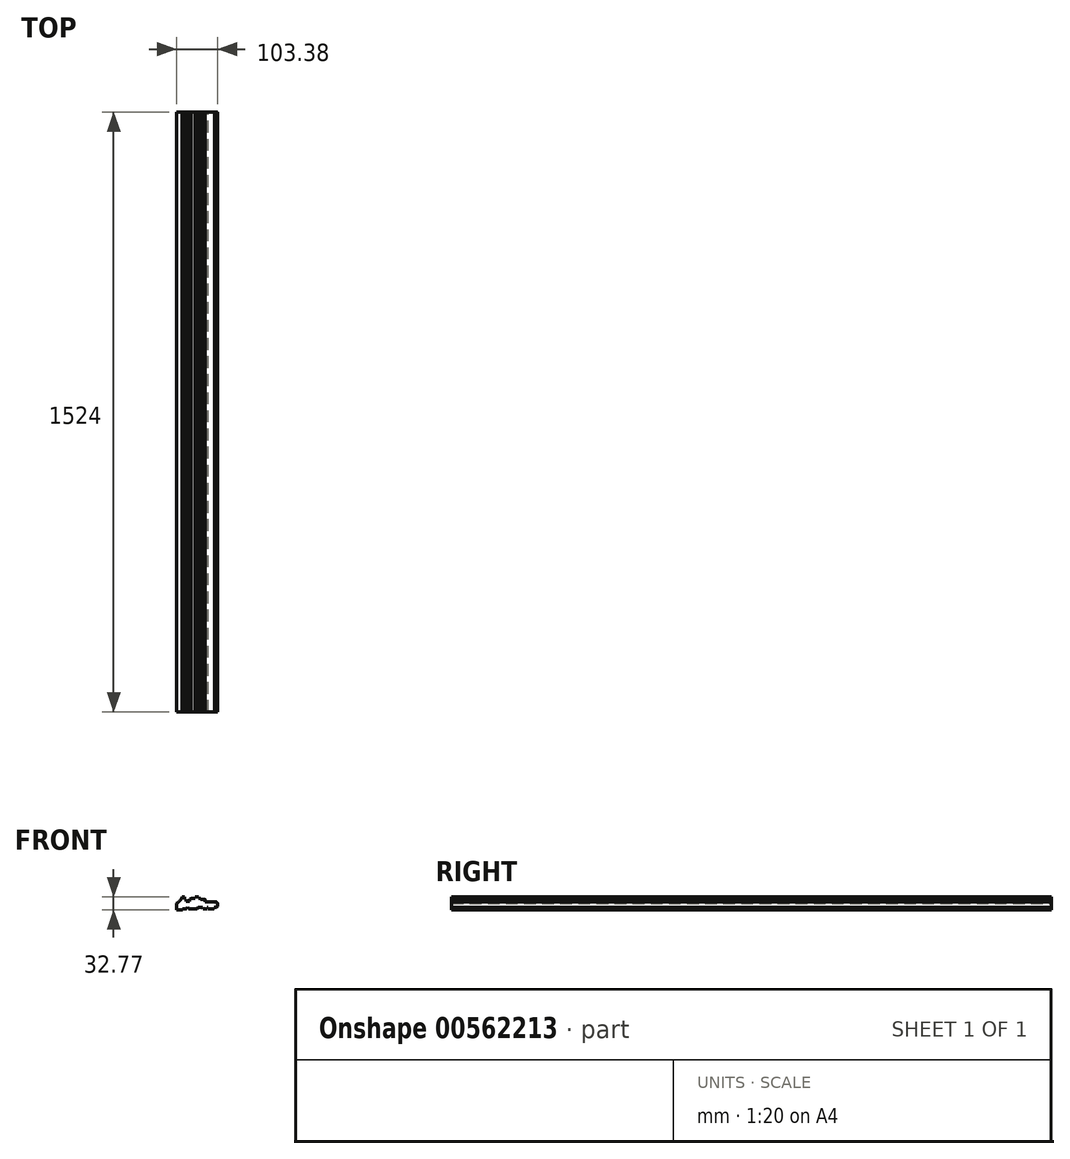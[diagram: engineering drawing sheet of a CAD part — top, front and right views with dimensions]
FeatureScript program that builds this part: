
annotation { "Feature Type Name" : "Feature", "Feature Type Description" : "" }
export const myFeature = defineFeature(function(context is Context, id is Id, definition is map)
    precondition{}
    {
        {
            var Q0;
            Q0=qCreatedBy(makeId("Front.planeOp"),FACE);
            var sketch = newSketch(context, id + "F0", { "sketchPlane" : qUnion([Q0])});
            skLineSegment(sketch, "E0", {"start": v(-88.77, 0) * mm, "end": v(-103.38, 0) * mm});
            skLineSegment(sketch, "E1", {"start": v(-103.38, 0) * mm, "end": v(-103.38, 16.8) * mm});
            skLineSegment(sketch, "E2", {"start": v(-88.77, 0) * mm, "end": v(-88.77, 2.08) * mm});
            skLineSegment(sketch, "E3", {"start": v(-88.77, 2.08) * mm, "end": v(-78.61, 2.08) * mm});
            skArc(sketch, "E4", {"start": v(-103.38, 16.8) * mm, "mid": v(-95.24, 23.3) * mm, "end": v(-90, 32.28) * mm});
            skLineSegment(sketch, "E5", {"start": v(-103.38, 16.8) * mm, "end": v(-90, 32.28) * mm, "construction": true});
            skLineSegment(sketch, "E6", {"start": v(-90, 32.28) * mm, "end": v(-83, 32.28) * mm});
            skLineSegment(sketch, "E7", {"start": v(-83, 32.28) * mm, "end": v(-83, 26.5) * mm});
            skLineSegment(sketch, "E8", {"start": v(-83, 26.5) * mm, "end": v(-80.16, 26.5) * mm});
            skLineSegment(sketch, "E9", {"start": v(-80.16, 26.5) * mm, "end": v(-80.16, 21.59) * mm});
            skLineSegment(sketch, "E10", {"start": v(-80.16, 21.59) * mm, "end": v(-70.38, 21.59) * mm});
            skLineSegment(sketch, "E11", {"start": v(-70.38, 21.59) * mm, "end": v(-70.38, 27.23) * mm});
            skLineSegment(sketch, "E12", {"start": v(-70.38, 27.23) * mm, "end": v(-66.95, 27.23) * mm});
            skLineSegment(sketch, "E13", {"start": v(-66.95, 27.23) * mm, "end": v(-66.95, 28.7) * mm});
            skLineSegment(sketch, "E14", {"start": v(-66.95, 28.7) * mm, "end": v(-56.8, 28.7) * mm});
            skLineSegment(sketch, "E15", {"start": v(-56.8, 28.7) * mm, "end": v(-56.8, 32.77) * mm});
            skLineSegment(sketch, "E16", {"start": v(-56.8, 32.77) * mm, "end": v(-48.51, 32.77) * mm});
            skLineSegment(sketch, "E17", {"start": v(-48.51, 32.77) * mm, "end": v(-48.51, 28.7) * mm});
            skLineSegment(sketch, "E18", {"start": v(-48.51, 28.7) * mm, "end": v(-42.55, 28.7) * mm});
            skLineSegment(sketch, "E19", {"start": v(-42.55, 28.7) * mm, "end": v(-42.55, 26.16) * mm});
            skLineSegment(sketch, "E20", {"start": v(-42.55, 26.16) * mm, "end": v(-39.37, 26.16) * mm});
            skLineSegment(sketch, "E21", {"start": v(-39.37, 26.16) * mm, "end": v(-39.37, 26.34) * mm});
            skLineSegment(sketch, "E22", {"start": v(-38.6, 27.1) * mm, "end": v(-32.47, 27.1) * mm});
            skLineSegment(sketch, "E23", {"start": v(-30.86, 25.49) * mm, "end": v(-30.86, 19.86) * mm});
            skLineSegment(sketch, "E24", {"start": v(-30.86, 19.86) * mm, "end": v(-7.87, 19.86) * mm});
            skLineSegment(sketch, "E25", {"start": v(0, 16.69) * mm, "end": v(0, 9.58) * mm});
            skLineSegment(sketch, "E26", {"start": v(-3.18, 6.4) * mm, "end": v(-4.58, 6.4) * mm});
            skLineSegment(sketch, "E27", {"start": v(-7.87, 6.4) * mm, "end": v(-7.87, 5.26) * mm});
            skPoint(sketch, "E28.visualSharp", {"position": v(-39.37, 27.1) * mm});
            skArc(sketch, "E28.filletArc", {"start": v(-38.6, 27.1) * mm, "mid": v(-39.15, 26.88) * mm, "end": v(-39.37, 26.34) * mm});
            skPoint(sketch, "E29.visualSharp", {"position": v(-30.86, 27.1) * mm});
            skArc(sketch, "E29.filletArc", {"start": v(-30.86, 25.49) * mm, "mid": v(-31.33, 26.63) * mm, "end": v(-32.47, 27.1) * mm});
            skPoint(sketch, "E30.visualSharp", {"position": v(0, 19.86) * mm});
            skArc(sketch, "E30.filletArc", {"start": v(0, 16.69) * mm, "mid": v(-0.93, 18.93) * mm, "end": v(-3.18, 19.86) * mm});
            skPoint(sketch, "E31.visualSharp", {"position": v(0, 6.4) * mm});
            skArc(sketch, "E31.filletArc", {"start": v(-3.18, 6.4) * mm, "mid": v(-0.93, 7.33) * mm, "end": v(0, 9.58) * mm});
            skLineSegment(sketch, "E32", {"start": v(-4.58, 6.4) * mm, "end": v(-4.58, 7.67) * mm});
            skLineSegment(sketch, "E33", {"start": v(-4.58, 7.67) * mm, "end": v(-7.87, 6.4) * mm});
            skLineSegment(sketch, "E34", {"start": v(-4.58, 19.86) * mm, "end": v(-4.58, 18.6) * mm});
            skLineSegment(sketch, "E35", {"start": v(-4.58, 18.6) * mm, "end": v(-7.87, 19.86) * mm});
            skPoint(sketch, "E36.newPointA", {"position": v(-7.87, 2.08) * mm});
            skPoint(sketch, "E36.newPointB", {"position": v(0, 2.08) * mm});
            skArc(sketch, "E36.filletArc", {"start": v(-11.05, 2.08) * mm, "mid": v(-8.8, 3.01) * mm, "end": v(-7.87, 5.26) * mm});
            skLineSegment(sketch, "E37.trimOffspring", {"start": v(-4.58, 19.86) * mm, "end": v(-3.18, 19.86) * mm});
            skLineSegment(sketch, "E38", {"start": v(-24.13, 2.08) * mm, "end": v(-24.13, 5.64) * mm});
            skLineSegment(sketch, "E39", {"start": v(-24.13, 5.64) * mm, "end": v(-26.67, 5.64) * mm});
            skLineSegment(sketch, "E40", {"start": v(-26.67, 5.64) * mm, "end": v(-26.67, 2.08) * mm});
            skLineSegment(sketch, "E41.trimOffspring", {"start": v(-24.13, 2.08) * mm, "end": v(-11.05, 2.08) * mm});
            skLineSegment(sketch, "E42", {"start": v(-38.35, 5.64) * mm, "end": v(-36.07, 2.08) * mm});
            skLineSegment(sketch, "E43", {"start": v(-38.35, 5.64) * mm, "end": v(-49.58, 5.64) * mm});
            skLineSegment(sketch, "E44", {"start": v(-49.58, 5.64) * mm, "end": v(-51.69, 2.08) * mm});
            skLineSegment(sketch, "E45", {"start": v(-78.61, 2.08) * mm, "end": v(-76.07, 8) * mm});
            skLineSegment(sketch, "E46", {"start": v(-76.07, 8) * mm, "end": v(-73.53, 2.08) * mm});
            skLineSegment(sketch, "E47.trimOffspring", {"start": v(-73.53, 2.08) * mm, "end": v(-51.69, 2.08) * mm});
            skLineSegment(sketch, "E48.trimOffspring", {"start": v(-36.07, 2.08) * mm, "end": v(-26.67, 2.08) * mm});
            skSolve(sketch);
        }
        {
            var Q0;
            Q0=makeQuery(id+"F0.imprint","IMPRINT",FACE,{"disambiguationData":[TD([[makeQuery(id+"F0.imprint","IMPRINT",EDGE,{"derivedFrom":sQuery(id+"F0.wireOp",EDGE,"E0")}),-1.0]])]});
            extrude(context, id + "F1", {"entities" : qUnion([Q0]), "depth" : 1524 * mm, "offsetDistance" : 25.4 * mm});
        }
    });
